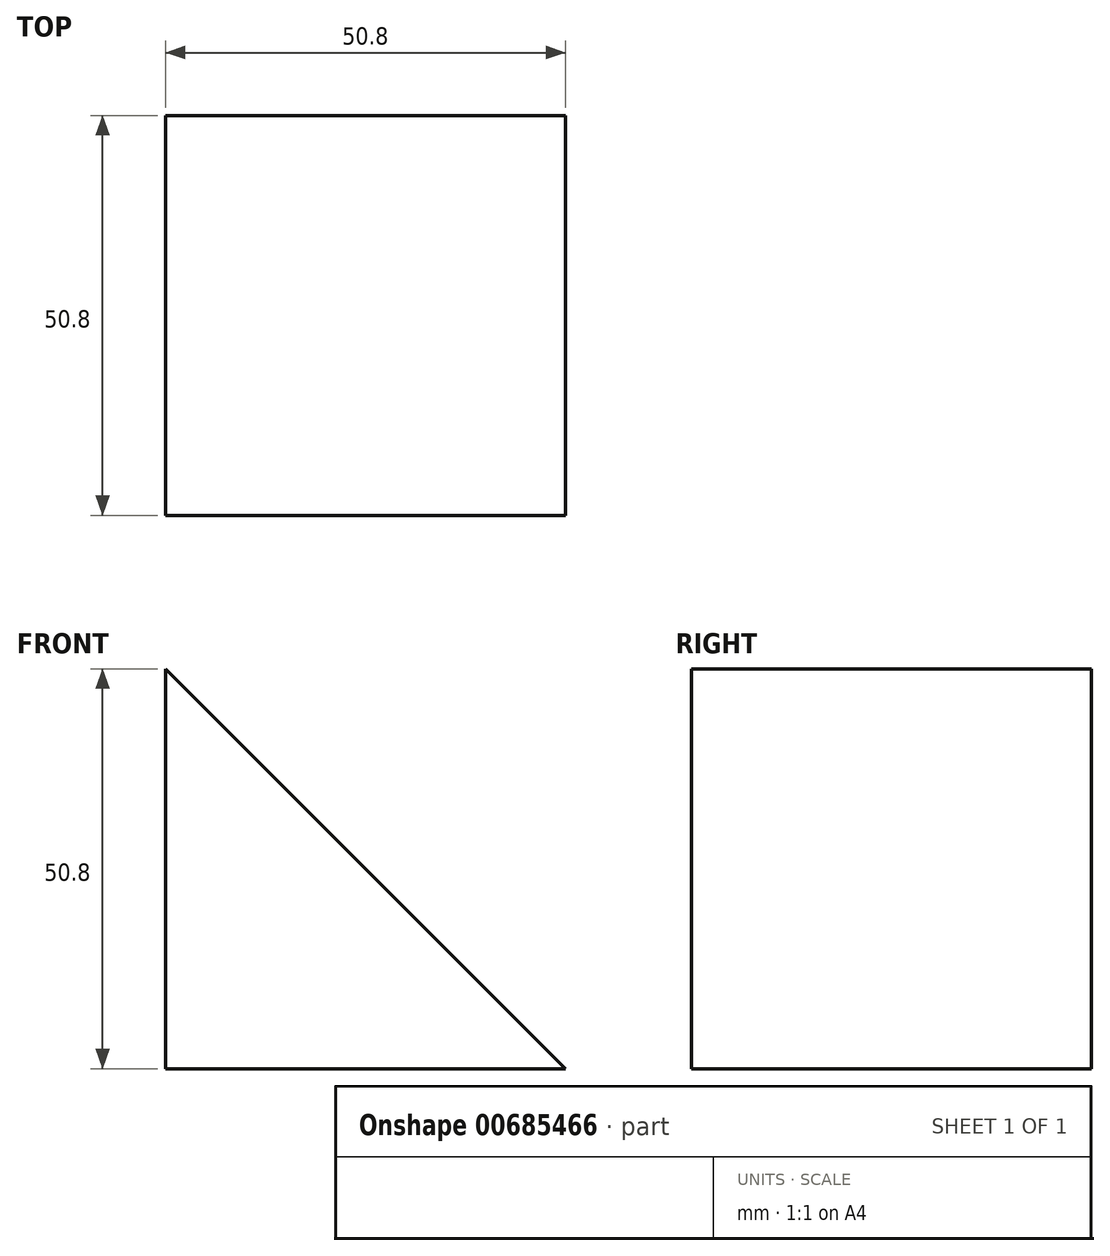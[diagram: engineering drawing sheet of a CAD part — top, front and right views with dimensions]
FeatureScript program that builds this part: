
annotation { "Feature Type Name" : "Feature", "Feature Type Description" : "" }
export const myFeature = defineFeature(function(context is Context, id is Id, definition is map)
    precondition{}
    {
        {
            var Q0;
            Q0=qCreatedBy(makeId("Front.planeOp"),FACE);
            var sketch = newSketch(context, id + "F0", { "sketchPlane" : qUnion([Q0])});
            skLineSegment(sketch, "E0", {"start": v(-42.1, 33.33) * mm, "end": v(-42.1, -17.47) * mm});
            skLineSegment(sketch, "E1", {"start": v(-42.1, -17.47) * mm, "end": v(8.7, -17.47) * mm});
            skLineSegment(sketch, "E2", {"start": v(8.7, -17.47) * mm, "end": v(-42.1, 33.33) * mm});
            skSolve(sketch);
        }
        {
            var Q0;
            Q0=makeQuery(id+"F0.imprint","IMPRINT",FACE,{"disambiguationData":[TD([[makeQuery(id+"F0.imprint","IMPRINT",EDGE,{"derivedFrom":sQuery(id+"F0.wireOp",EDGE,"E0")}),1.0]])]});
            extrude(context, id + "F1", {"entities" : qUnion([Q0]), "depth" : 50.8 * mm, "offsetDistance" : 25.4 * mm});
        }
    });
